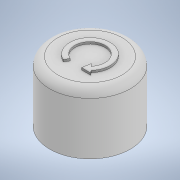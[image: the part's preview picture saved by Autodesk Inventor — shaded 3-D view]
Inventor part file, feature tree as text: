
AUTODESK INVENTOR PART (.ipt)
format: ipt  version: 2021 (Build 250183000, 183)  size: 139,264 bytes
history: native  units: in
note: dims shown in document units (in); Inventor stores cm internally (conversion verified against a paired STEP export)
features: extrude x3, sketch x3, fillet x1
ambient origin geometry x8: Origin, YZ Plane, XZ Plane, XY Plane, X Axis, Y Axis, Z Axis, Center Point
bodies: Solid1 (feature_tree)
feature tree (7):
  extrude  "Extrusion1"  Depth=0.5906in TaperAngle=0.0deg
  extrude  "Extrusion2"  Depth=0.1969in TaperAngle=0.0deg
  fillet  "Fillet1"  Radius=0.0787in
  extrude  "Extrusion4"  Depth=0.3937in
  sketch  "Sketch1"  dims[d0=0.7874in d1=0.5906in d2=0.0in]
  sketch  "Sketch2"  dims[d3=0.5906in d4=0.1969in d5=0.0in d6=0.0787in]
  sketch  "Sketch4"  dims[d12=0.2953in d13=0.3937in d14=0.0197in d15=0.0in]
